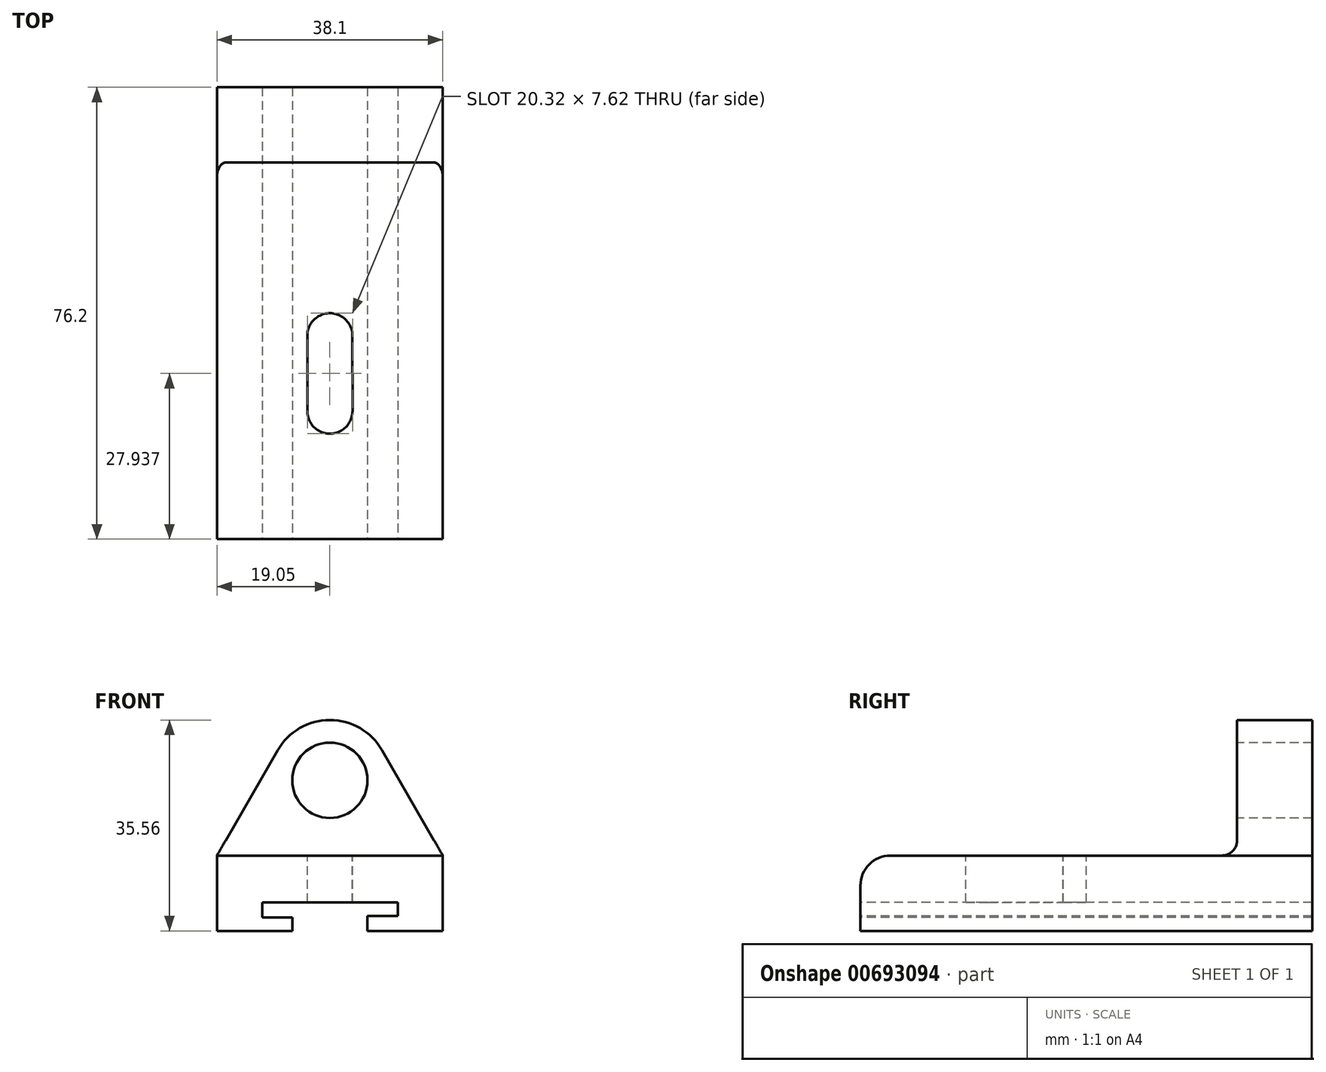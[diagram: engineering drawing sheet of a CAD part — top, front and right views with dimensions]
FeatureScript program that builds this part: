
annotation { "Feature Type Name" : "Feature", "Feature Type Description" : "" }
export const myFeature = defineFeature(function(context is Context, id is Id, definition is map)
    precondition{}
    {
        {
            var Q0;
            Q0=qCreatedBy(makeId("Right.planeOp"),FACE);
            var sketch = newSketch(context, id + "F0", { "sketchPlane" : qUnion([Q0])});
            skLineSegment(sketch, "E0", {"start": v(0, 0) * mm, "end": v(-51.15, 0) * mm});
            skLineSegment(sketch, "E1", {"start": v(-51.15, 0) * mm, "end": v(-51.15, 12.7) * mm});
            skLineSegment(sketch, "E2", {"start": v(-51.15, 12.7) * mm, "end": v(12.35, 12.7) * mm});
            skLineSegment(sketch, "E3", {"start": v(12.35, 12.7) * mm, "end": v(12.35, 38.1) * mm});
            skLineSegment(sketch, "E4", {"start": v(12.35, 38.1) * mm, "end": v(25.05, 38.1) * mm});
            skLineSegment(sketch, "E5", {"start": v(25.05, 38.1) * mm, "end": v(25.05, 0) * mm});
            skLineSegment(sketch, "E6", {"start": v(25.05, 0) * mm, "end": v(0, 0) * mm});
            skSolve(sketch);
        }
        {
            var Q0;
            Q0 = qSketchRegion(id + "F0", true);
            extrude(context, id + "F1", {"entities" : qUnion([Q0]), "endBound" : BoundingType.SYMMETRIC, "depth" : 38.1 * mm, "offsetDistance" : 25.4 * mm});
        }
        {
            var Q0;
            Q0=makeQuery(id+"F1.opExtrude","SWEPT_FACE",FACE,{"disambiguationData":[OSD([sQuery(id+"F0.wireOp",EDGE,"E3")])]});
            var sketch = newSketch(context, id + "F2", { "sketchPlane" : qUnion([Q0])});
            skArc(sketch, "E7", {"start": v(8.8, 30.47) * mm, "mid": v(0, 35.56) * mm, "end": v(-8.8, 30.47) * mm});
            skLineSegment(sketch, "E8", {"start": v(-19.05, 12.7) * mm, "end": v(-8.8, 30.47) * mm});
            skLineSegment(sketch, "E9", {"start": v(19.05, 12.7) * mm, "end": v(8.8, 30.47) * mm});
            skSolve(sketch);
        }
        {
            var Q0;
            Q0 = qSketchRegion(id + "F2", true);
            var Q1;
            Q1=makeQuery(id+"F2.imprint","IMPRINT",FACE,{"disambiguationData":[TD([[makeQuery(id+"F2.imprint","IMPRINT",EDGE,{"derivedFrom":sQuery(id+"F2.wireOp",EDGE,"E7")}),-1.0]])]});
            extrude(context, id + "F3", {"entities" : qUnion([Q0, Q1]), "operationType" : NewBodyOperationType.REMOVE, "endBound" : BoundingType.THROUGH_ALL, "oppositeDirection" : true, "depth" : 25.4 * mm, "offsetDistance" : 25.4 * mm});
        }
        {
            var Q0;
            Q0=makeQuery(id+"F1.opExtrude","SWEPT_FACE",FACE,{"disambiguationData":[OSD([sQuery(id+"F0.wireOp",EDGE,"E3")])]});
            var sketch = newSketch(context, id + "F4", { "sketchPlane" : qUnion([Q0])});
            skCircle(sketch, "E10", {"center": v(0, 25.4) * mm, "radius": 6.35 * mm});
            skSolve(sketch);
        }
        {
            var Q0;
            Q0 = qSketchRegion(id + "F4", true);
            extrude(context, id + "F5", {"entities" : qUnion([Q0]), "operationType" : NewBodyOperationType.REMOVE, "endBound" : BoundingType.THROUGH_ALL, "oppositeDirection" : true, "depth" : 25.4 * mm, "offsetDistance" : 25.4 * mm});
        }
        {
            var Q0;
            Q0=makeQuery(id+"F1.opExtrude","SWEPT_EDGE",EDGE,{"disambiguationData":[OSD([sQuery(id+"F0.wireOp",EDGE,"E2"),sQuery(id+"F0.wireOp",EDGE,"E3")])]});
            fillet(context, id + "F6", {"entities" : qUnion([Q0]), "radius" : 2.54 * mm, "tangentPropagation" : true, "allowEdgeOverflow" : false});
        }
        {
            var Q0;
            Q0=makeQuery(id+"F1.opExtrude","SWEPT_FACE",FACE,{"disambiguationData":[OSD([sQuery(id+"F0.wireOp",EDGE,"E1")])]});
            var sketch = newSketch(context, id + "F7", { "sketchPlane" : qUnion([Q0])});
            skLineSegment(sketch, "E11", {"start": v(0, 0) * mm, "end": v(-6.35, 0) * mm});
            skLineSegment(sketch, "E12", {"start": v(-6.35, 0) * mm, "end": v(-6.35, 2.27) * mm});
            skLineSegment(sketch, "E13", {"start": v(-6.35, 2.27) * mm, "end": v(-11.43, 2.27) * mm});
            skLineSegment(sketch, "E14", {"start": v(-11.43, 2.27) * mm, "end": v(-11.43, 4.8) * mm});
            skLineSegment(sketch, "E15", {"start": v(-11.43, 4.8) * mm, "end": v(11.43, 4.8) * mm});
            skLineSegment(sketch, "E16", {"start": v(11.43, 4.8) * mm, "end": v(11.43, 2.5) * mm});
            skLineSegment(sketch, "E17", {"start": v(11.43, 2.5) * mm, "end": v(6.35, 2.5) * mm});
            skLineSegment(sketch, "E18", {"start": v(6.35, 2.5) * mm, "end": v(6.35, 0) * mm});
            skSolve(sketch);
        }
        {
            var Q0;
            Q0 = qSketchRegion(id + "F7", true);
            var Q1;
            {var subQ0=sQuery(id+"F7.wireOp",EDGE,"E11");Q1=makeQuery(id+"F7.imprint","IMPRINT",FACE,{"disambiguationData":[TD([[makeQuery(id+"F7.imprint","IMPRINT",EDGE,{"derivedFrom":subQ0}),-1.0]])]});}
            extrude(context, id + "F8", {"entities" : qUnion([Q0, Q1]), "operationType" : NewBodyOperationType.REMOVE, "endBound" : BoundingType.THROUGH_ALL, "oppositeDirection" : true, "depth" : 25.4 * mm, "offsetDistance" : 25.4 * mm});
        }
        {
            var Q0;
            Q0=makeQuery(id+"F1.opExtrude","SWEPT_EDGE",EDGE,{"disambiguationData":[OSD([sQuery(id+"F0.wireOp",EDGE,"E1"),sQuery(id+"F0.wireOp",EDGE,"E2")])]});
            fillet(context, id + "F9", {"entities" : qUnion([Q0]), "radius" : 5.08 * mm, "tangentPropagation" : true, "allowEdgeOverflow" : false});
        }
        {
            var Q0;
            Q0=makeQuery(id+"F1.opExtrude","SWEPT_FACE",FACE,{"disambiguationData":[OSD([sQuery(id+"F0.wireOp",EDGE,"E2")])]});
            var sketch = newSketch(context, id + "F10", { "sketchPlane" : qUnion([Q0])});
            skArc(sketch, "E19", {"start": v(3.8, -16.98) * mm, "mid": v(0.02, -13.05) * mm, "end": v(-3.8, -16.94) * mm});
            skArc(sketch, "E20", {"start": v(-3.8, -29.56) * mm, "mid": v(0, -33.37) * mm, "end": v(3.8, -29.56) * mm});
            skLineSegment(sketch, "E21", {"start": v(3.8, -16.74) * mm, "end": v(3.8, -29.56) * mm});
            skLineSegment(sketch, "E22", {"start": v(-3.8, -16.78) * mm, "end": v(-3.8, -29.56) * mm});
            skSolve(sketch);
        }
        {
            var Q0;
            Q0 = qSketchRegion(id + "F10", true);
            extrude(context, id + "F11", {"entities" : qUnion([Q0]), "operationType" : NewBodyOperationType.REMOVE, "oppositeDirection" : true, "depth" : 25.4 * mm, "offsetDistance" : 25.4 * mm});
        }
    });
